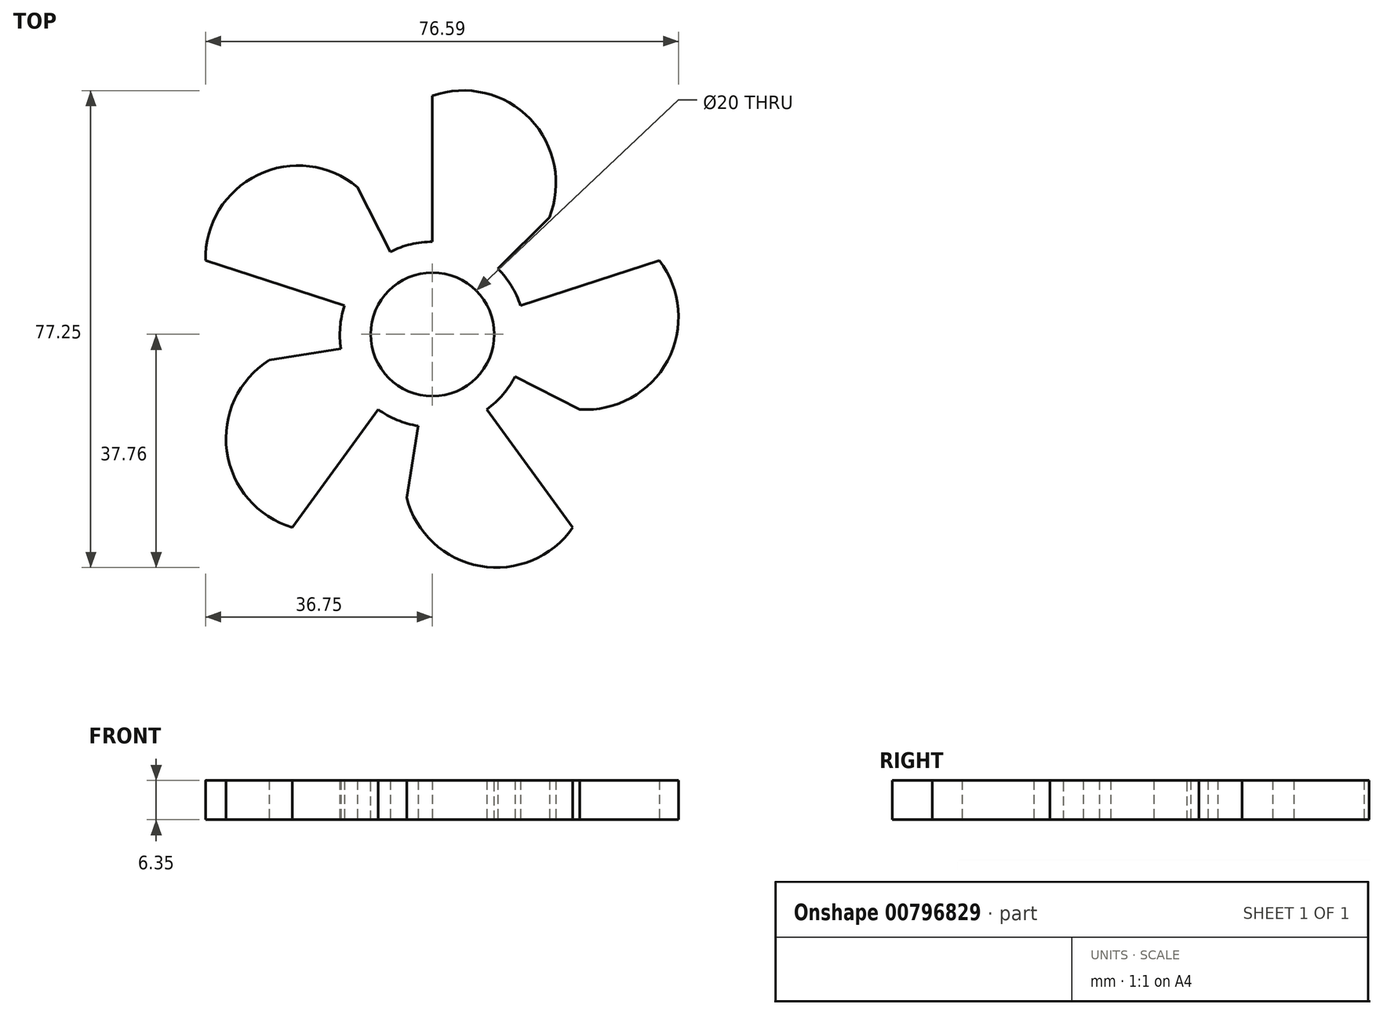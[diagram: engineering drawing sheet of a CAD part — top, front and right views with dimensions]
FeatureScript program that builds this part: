
annotation { "Feature Type Name" : "Feature", "Feature Type Description" : "" }
export const myFeature = defineFeature(function(context is Context, id is Id, definition is map)
    precondition{}
    {
        {
            var Q0;
            Q0=qCreatedBy(makeId("Top.planeOp"),FACE);
            var sketch = newSketch(context, id + "F0", { "sketchPlane" : qUnion([Q0])});
            skLineSegment(sketch, "E0", {"start": v(0, 0) * mm, "end": v(0, 38.64) * mm});
            skArc(sketch, "E1", {"start": v(18.93, 18.93) * mm, "mid": v(15.82, 34.89) * mm, "end": v(0, 38.64) * mm});
            skLineSegment(sketch, "E2", {"start": v(18.93, 18.93) * mm, "end": v(0, 0) * mm});
            skSolve(sketch);
        }
        {
            var Q0;
            Q0=makeQuery(id+"F0.imprint","IMPRINT",FACE,{"disambiguationData":[TD([[makeQuery(id+"F0.imprint","IMPRINT",EDGE,{"derivedFrom":sQuery(id+"F0.wireOp",EDGE,"E0")}),-1.0]])]});
            extrude(context, id + "F1", {"entities" : qUnion([Q0]), "depth" : 6.35 * mm, "offsetDistance" : 25.4 * mm});
        }
        {
            var Q0;
            Q0=makeQuery(id+"F1.opExtrude","SWEPT_BODY",BODY,{"disambiguationData":[OSD([sQuery(id+"F0.wireOp",EDGE,"E0"),sQuery(id+"F0.wireOp",EDGE,"E1"),sQuery(id+"F0.wireOp",EDGE,"E2")])]});
            var Q1;
            Q1=makeQuery(id+"F1.opExtrude","SWEPT_EDGE",EDGE,{"disambiguationData":[OSD([sQuery(id+"F0.wireOp",EDGE,"E0"),sQuery(id+"F0.wireOp",EDGE,"E2")])]});
            circularPattern(context, id + "F2", {"entities" : qUnion([Q0]), "axis" : qUnion([Q1]), "angle" : 360 * degree, "instanceCount" : 5, "equalSpace" : true});
        }
        {
            var Q0;
            Q0=qCreatedBy(makeId("Top.planeOp"),FACE);
            var sketch = newSketch(context, id + "F3", { "sketchPlane" : qUnion([Q0])});
            skCircle(sketch, "E3", {"center": v(0, 0) * mm, "radius": 15 * mm});
            skSolve(sketch);
        }
        {
            var Q0;
            Q0=makeQuery(id+"F3.imprint","IMPRINT",FACE,{"disambiguationData":[TD([[makeQuery(id+"F3.imprint","IMPRINT",EDGE,{"derivedFrom":sQuery(id+"F3.wireOp",EDGE,"E3")}),1.0]])]});
            var Q1;
            Q1=makeQuery(id+"F2.opPattern","COPY",FACE,{"derivedFrom":makeQuery(id+"F1.opExtrude","CAP_FACE",FACE,{"disambiguationData":[OSD([sQuery(id+"F0.wireOp",EDGE,"E0"),sQuery(id+"F0.wireOp",EDGE,"E1"),sQuery(id+"F0.wireOp",EDGE,"E2")])],"isStart":false}),"instanceName":"2"});
            extrude(context, id + "F4", {"entities" : qUnion([Q0]), "operationType" : NewBodyOperationType.ADD, "endBound" : BoundingType.UP_TO_SURFACE, "depth" : 25 * mm, "endBoundEntityFace" : qUnion([Q1]), "offsetDistance" : 25 * mm});
        }
        {
            var Q0;
            {var subQ0=sQuery(id+"F0.wireOp",EDGE,"E2");var subQ1=sQuery(id+"F0.wireOp",EDGE,"E1");var subQ2=sQuery(id+"F0.wireOp",EDGE,"E0");var subQ3=makeQuery(id+"F1.opExtrude","CAP_FACE",FACE,{"disambiguationData":[OSD([subQ2,subQ1,subQ0])],"isStart":false});Q0=makeQuery(id+"F4.boolean.opBoolean","MERGE",FACE,{"derivedFrom":[subQ3,makeQuery(id+"F2.opPattern","COPY",FACE,{"derivedFrom":subQ3,"instanceName":"1"}),makeQuery(id+"F2.opPattern","COPY",FACE,{"derivedFrom":subQ3,"instanceName":"2"}),makeQuery(id+"F2.opPattern","COPY",FACE,{"derivedFrom":subQ3,"instanceName":"3"}),makeQuery(id+"F2.opPattern","COPY",FACE,{"derivedFrom":subQ3,"instanceName":"4"}),makeQuery(id+"F4.opExtrude","CAP_FACE",FACE,{"disambiguationData":[OSD([subQ2,subQ1,subQ0])],"isStart":false})]});}
            var sketch = newSketch(context, id + "F5", { "sketchPlane" : qUnion([Q0])});
            skCircle(sketch, "E4", {"center": v(0, 0) * mm, "radius": 10 * mm});
            skSolve(sketch);
        }
        {
            var Q0;
            Q0 = qSketchRegion(id + "F5", true);
            extrude(context, id + "F6", {"entities" : qUnion([Q0]), "operationType" : NewBodyOperationType.REMOVE, "endBound" : BoundingType.THROUGH_ALL, "oppositeDirection" : true, "depth" : 25 * mm, "offsetDistance" : 25 * mm});
        }
    });
